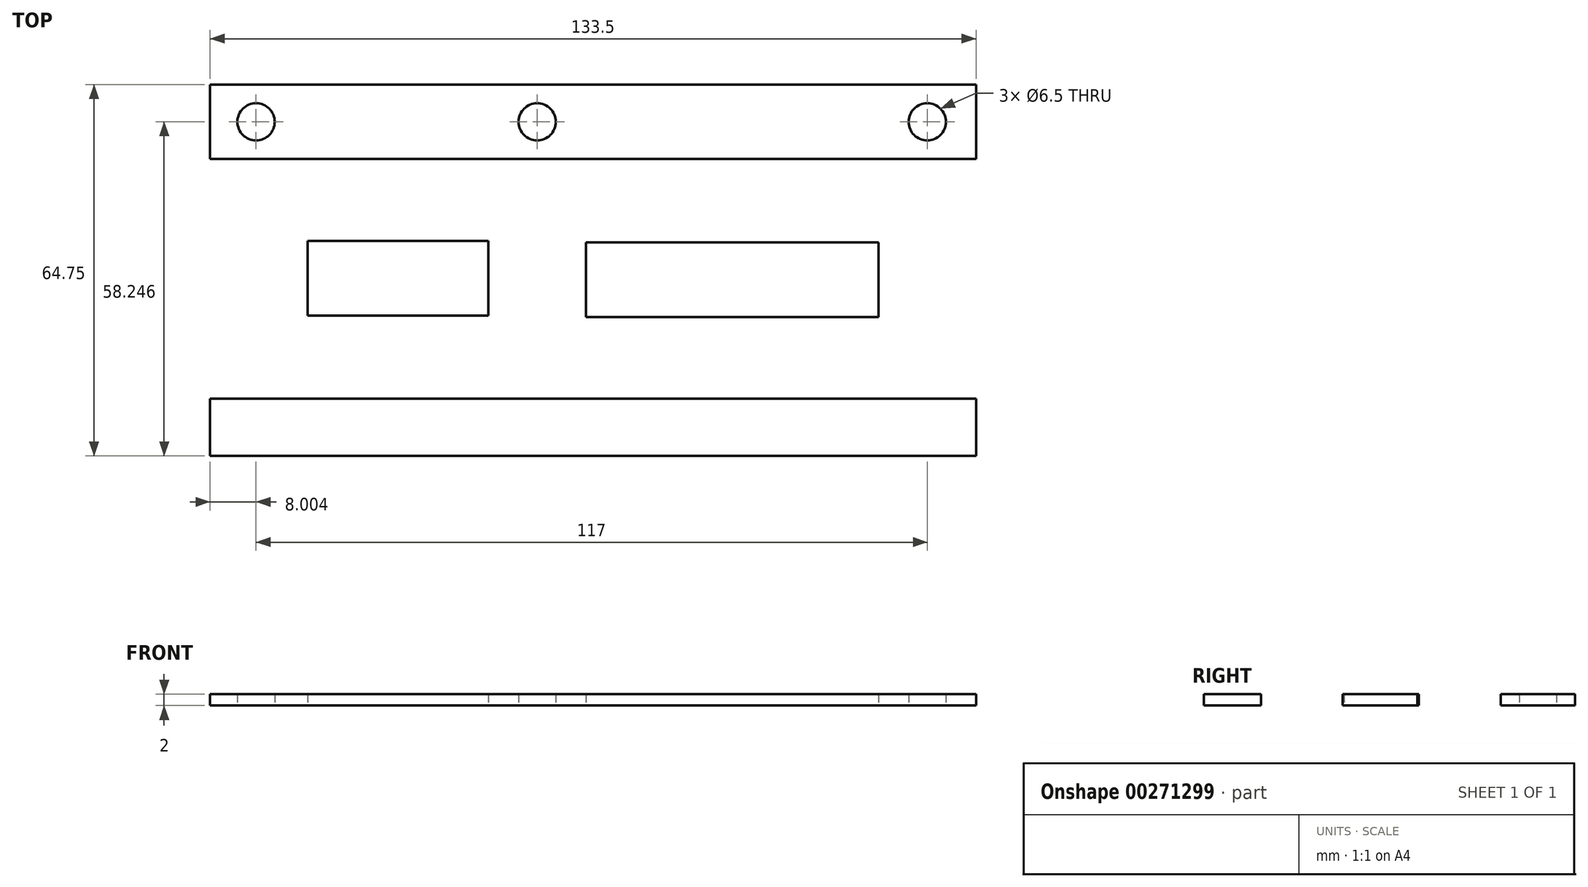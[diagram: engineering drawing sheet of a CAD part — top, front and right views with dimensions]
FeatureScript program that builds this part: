
annotation { "Feature Type Name" : "Feature", "Feature Type Description" : "" }
export const myFeature = defineFeature(function(context is Context, id is Id, definition is map)
    precondition{}
    {
        {
            var Q0;
            Q0=qCreatedBy(makeId("Top.planeOp"),FACE);
            var sketch = newSketch(context, id + "F0", { "sketchPlane" : qUnion([Q0])});
            skLineSegment(sketch, "E0.bottom", {"start": v(-43.22, 28.29) * mm, "end": v(90.28, 28.29) * mm});
            skLineSegment(sketch, "E0.top", {"start": v(-43.22, 15.29) * mm, "end": v(90.28, 15.29) * mm});
            skLineSegment(sketch, "E0.left", {"start": v(-43.22, 28.29) * mm, "end": v(-43.22, 15.29) * mm});
            skLineSegment(sketch, "E0.right", {"start": v(90.28, 28.29) * mm, "end": v(90.28, 15.29) * mm});
            skCircle(sketch, "E1", {"center": v(-35.22, 21.79) * mm, "radius": 3.25 * mm});
            skCircle(sketch, "E2", {"center": v(13.78, 21.79) * mm, "radius": 3.25 * mm});
            skCircle(sketch, "E3", {"center": v(81.78, 21.79) * mm, "radius": 3.25 * mm});
            skLineSegment(sketch, "E4.bottom", {"start": v(-43.22, 15.29) * mm, "end": v(-26.22, 15.29) * mm});
            skLineSegment(sketch, "E4.left", {"start": v(-43.22, 15.29) * mm, "end": v(-43.22, -26.46) * mm});
            skLineSegment(sketch, "E4.right", {"start": v(-26.22, 15.29) * mm, "end": v(-26.22, -26.46) * mm});
            skLineSegment(sketch, "E5.bottom", {"start": v(5.28, 15.29) * mm, "end": v(22.28, 15.29) * mm});
            skLineSegment(sketch, "E5.left", {"start": v(5.28, 15.29) * mm, "end": v(5.28, -26.46) * mm});
            skLineSegment(sketch, "E5.right", {"start": v(22.28, 15.29) * mm, "end": v(22.28, -26.46) * mm});
            skLineSegment(sketch, "E6.bottom", {"start": v(73.28, 15.29) * mm, "end": v(90.28, 15.29) * mm});
            skLineSegment(sketch, "E6.left", {"start": v(73.28, 15.29) * mm, "end": v(73.28, -26.46) * mm});
            skLineSegment(sketch, "E6.right", {"start": v(90.28, 15.29) * mm, "end": v(90.28, -26.46) * mm});
            skLineSegment(sketch, "E7", {"start": v(22.28, -12.21) * mm, "end": v(73.28, -12.21) * mm});
            skLineSegment(sketch, "E8", {"start": v(5.28, -11.96) * mm, "end": v(-26.22, -11.96) * mm});
            skLineSegment(sketch, "E9", {"start": v(-43.22, -26.46) * mm, "end": v(90.28, -26.46) * mm});
            skLineSegment(sketch, "E10", {"start": v(-43.22, -36.46) * mm, "end": v(90.28, -36.46) * mm});
            skLineSegment(sketch, "E11", {"start": v(-43.22, -26.46) * mm, "end": v(-43.22, -36.46) * mm});
            skLineSegment(sketch, "E12", {"start": v(90.28, -26.46) * mm, "end": v(90.28, -36.46) * mm});
            skCircle(sketch, "E13", {"center": v(-35.22, 0.79) * mm, "radius": 3.25 * mm});
            skCircle(sketch, "E14", {"center": v(13.78, 0.79) * mm, "radius": 3.25 * mm});
            skPoint(sketch, "E14.centerSnap0", {"position": v(13.78, 15.29) * mm});
            skCircle(sketch, "E15", {"center": v(81.78, 0.79) * mm, "radius": 3.25 * mm});
            skCircle(sketch, "E16", {"center": v(-35.22, -19.21) * mm, "radius": 3.25 * mm});
            skLineSegment(sketch, "E17", {"start": v(-26.22, 1.04) * mm, "end": v(5.28, 1.04) * mm});
            skLineSegment(sketch, "E18", {"start": v(22.28, 0.79) * mm, "end": v(73.28, 0.79) * mm});
            skCircle(sketch, "E19", {"center": v(13.78, -19.21) * mm, "radius": 3.25 * mm});
            skCircle(sketch, "E20", {"center": v(81.78, -19.21) * mm, "radius": 3.25 * mm});
            skSolve(sketch);
        }
        {
            var Q0;
            {var subQ3=sQuery(id+"F0.wireOp",EDGE,"E4.bottom");Q0=makeQuery(id+"F0.imprint","IMPRINT",FACE,{"disambiguationData":[TD([[makeQuery(id+"F0.imprint","IMPRINT",EDGE,{"derivedFrom":subQ3}),-1.0]])]});}
            var Q1;
            {var subQ0=sQuery(id+"F0.wireOp",EDGE,"lsAsrtjf-JJFr-xZpy-lqfN-q9Sr91RTCNLR");Q1=makeQuery(id+"F0.imprint","IMPRINT",FACE,{"disambiguationData":[TD([[makeQuery(id+"F0.imprint","IMPRINT",EDGE,{"derivedFrom":subQ0}),-1.0]])]});}
            var Q2;
            {var subQ5=sQuery(id+"F0.wireOp",EDGE,"E5.bottom");Q2=makeQuery(id+"F0.imprint","IMPRINT",FACE,{"disambiguationData":[TD([[makeQuery(id+"F0.imprint","IMPRINT",EDGE,{"derivedFrom":subQ5}),-1.0]])]});}
            var Q3;
            {var subQ0=sQuery(id+"F0.wireOp",EDGE,"b4I5HeD3-6ek1-SCvf-ctWl-cBr5lzd9Sy1M");Q3=makeQuery(id+"F0.imprint","IMPRINT",FACE,{"disambiguationData":[TD([[makeQuery(id+"F0.imprint","IMPRINT",EDGE,{"derivedFrom":subQ0}),-1.0]])]});}
            var Q4;
            {var subQ5=sQuery(id+"F0.wireOp",EDGE,"E6.bottom");Q4=makeQuery(id+"F0.imprint","IMPRINT",FACE,{"disambiguationData":[TD([[makeQuery(id+"F0.imprint","IMPRINT",EDGE,{"derivedFrom":subQ5}),-1.0]])]});}
            var Q5;
            Q5=makeQuery(id+"F0.imprint","IMPRINT",FACE,{"disambiguationData":[TD([[makeQuery(id+"F0.imprint","IMPRINT",EDGE,{"derivedFrom":sQuery(id+"F0.wireOp",EDGE,"E10")}),1.0]])]});
            var Q6;
            {var subQ0=sQuery(id+"F0.wireOp",EDGE,"E8");Q6=makeQuery(id+"F0.imprint","IMPRINT",FACE,{"disambiguationData":[TD([[makeQuery(id+"F0.imprint","IMPRINT",EDGE,{"derivedFrom":subQ0}),-1.0]])]});}
            var Q7;
            {var subQ0=sQuery(id+"F0.wireOp",EDGE,"E7");Q7=makeQuery(id+"F0.imprint","IMPRINT",FACE,{"disambiguationData":[TD([[makeQuery(id+"F0.imprint","IMPRINT",EDGE,{"derivedFrom":subQ0}),1.0]])]});}
            extrude(context, id + "F1", {"entities" : qUnion([Q0, Q1, Q2, Q3, Q4, Q5, Q6, Q7]), "depth" : 2 * mm});
        }
        {
            var Q0;
            Q0=makeQuery(id+"F0.imprint","IMPRINT",FACE,{"disambiguationData":[TD([[makeQuery(id+"F0.imprint","IMPRINT",EDGE,{"derivedFrom":sQuery(id+"F0.wireOp",EDGE,"E0.bottom")}),-1.0]])]});
            extrude(context, id + "F2", {"entities" : qUnion([Q0]), "operationType" : NewBodyOperationType.ADD, "depth" : 2 * mm});
        }
    });
